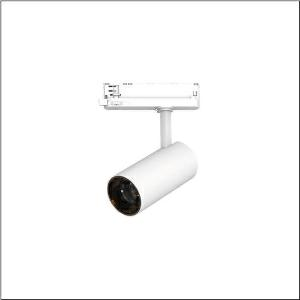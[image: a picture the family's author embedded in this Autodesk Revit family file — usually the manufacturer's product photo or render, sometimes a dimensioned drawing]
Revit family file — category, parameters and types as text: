
# Revit family: spot_31_slim_51sf137fa2b
name_source: partatom
category: Lighting Fixtures
units: mm (PartAtom-declared; Revit-internal decimal feet)

## family parameters
Cut with Voids When Loaded = No
Host = Face
Light Source = No
Part Type = Normal
Room Calculation Point = No
Round Connector Dimension = Use Diameter
Shared = No

## types (1)
- Spot 31 Slim (1 x LED, 2150 lm, 17.6 W, 2700K)
    Apparent Load = 18 VA
    CIE Flux Codes = 97 100 100 100 100
    Color Rendering = 90
    Color Temperature = 2700K
    Default Elevation = 1800 mm
    Description = Spot 31 Slim, directional spotlight, light control with reflector, of aluminium, LED rated luminous flux: 2.150lm, light colour: 927, control gear: ECG, with 3-phase adapter, mains connection: 220..240V, AC, 50/60Hz, housing, of aluminium, traffic white (RAL 9016), diameter: 70mm, adapter, of plastic, protection rating (complete): IP20, insulation class (complete): insulation class I (protective earthing), certification: CE, impact resistance: IK02, packaging unit: 1 piece
    Height = 210 mm
    Lamp = 1 x LED
    Lamp Light Flux = 2150 lm
    Lamp Power = 17.6 W
    Lamp count = 1
    Length = 70 mm
    Luminous efficacy = 122 lm/W
    Manufacturer = Siteco
    ModVariant = No
    Model = 51SF137FA2B
    Mounting Place = Ceiling
    Mounting Type = Pendant
    Number of Poles = 1
    OnlyDefault = Yes
    Power Factor = 1
    Product Name = Spot 31 Slim
    Product group = directional spotlight
    ProductGroupID = 905
    Protection Class = Protection class I
    Protection Degree = IP 20
    RLX_Detail_Level = 1
    RLX_Emergency_Light_Flux = 0 lm
    RLX_Emergency_Type = 0
    RLX_Emergency_Type_DB = No
    RlxData = <blob elided: 14149 chars, md5=5393402c>
    Socket = socket
    Standby Power = 0 W
    System Light Flux = 2150 lm
    System Power = 18 W
    Type Comments = Product without accessories
    Type Image = l_1228468.jpg
    URL = http://relux.com
    VarID = ---
    Voltage = 0 V
    Weight = 0.00 kg
    Width = 0 mm  [stored 0 ft]

note: [stored X ft] marks values corroborated as IEEE doubles in the binary element streams (Revit-internal decimal feet)

## geometry (parser evidence)
native form markers: Sweep x12
no freeform markers — native parametric forms only
